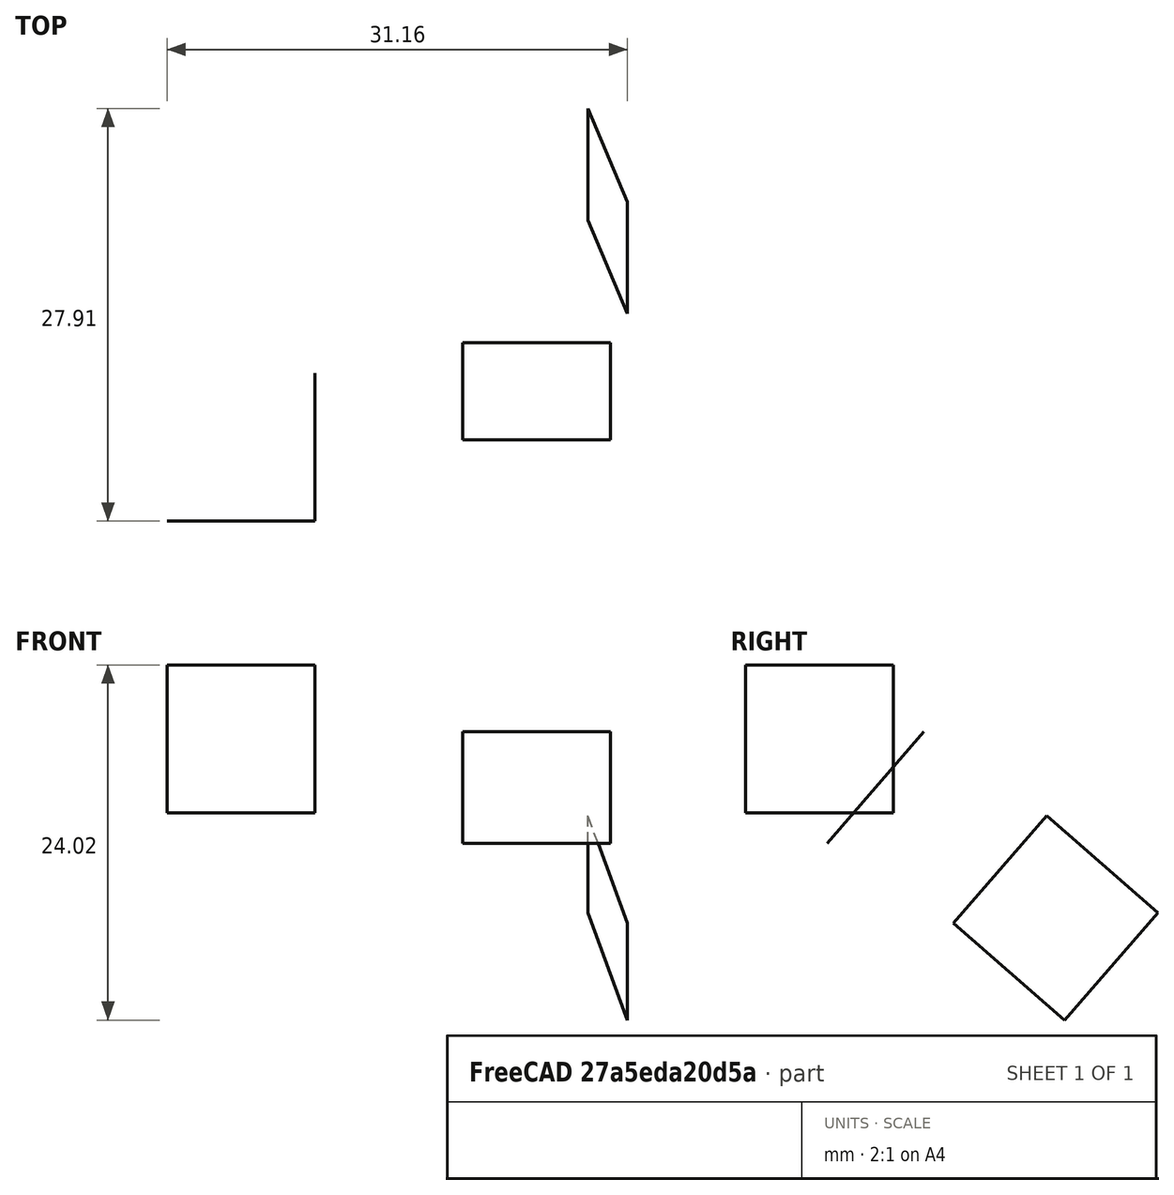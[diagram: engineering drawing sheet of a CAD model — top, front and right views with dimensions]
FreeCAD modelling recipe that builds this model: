
FCSTD DOCUMENT  (FreeCAD 0.19R17089 +1543 (Git))
Label: rt-super-2-c
License: All rights reserved
LicenseURL: http://en.wikipedia.org/wiki/All_rights_reserved
objects: App::FeaturePython×13, Part::FeaturePython×9, App::LinkElement×4, App::Link×1
note: 8 computed .brp shape members not serialized (recipe doc carries the construction recipe); baked Part::Feature solids carry a one-line shape summary decoded from their .brp
EXTERNAL_REF file=rt-super-2-a.FCStd obj=Assembly

FEATURE [App::LinkElement] Link_i0
  LinkedObject = -> <external rt-super-2-a.FCStd>#Assembly
FEATURE [App::LinkElement] Link_i1
  LinkPlacement = pos=(25,4.4e-15,5) rot=(0.672999,0.30683,-0.672999;3.73701rad)
  LinkedObject = -> <external rt-super-2-a.FCStd>#Assembly
  Placement = pos=(25,4.4e-15,5) rot=(0.672999,0.30683,-0.672999;3.73701rad)
FEATURE [App::LinkElement] Link_i2
  LinkPlacement = pos=(20,18.8729,-11.3956) rot=(-0.950073,0.12944,-0.283912;5.38835rad)
  LinkedObject = -> <external rt-super-2-a.FCStd>#Assembly
  Placement = pos=(20,18.8729,-11.3956) rot=(-0.950073,0.12944,-0.283912;5.38835rad)
FEATURE [App::LinkElement] Link_i3
  LinkPlacement = pos=(44.0888,19.4844,-3.06764) rot=(-0.167621,-0.947396,0.272662;1.8739rad)
  LinkedObject = -> <external rt-super-2-a.FCStd>#Assembly
  Placement = pos=(44.0888,19.4844,-3.06764) rot=(-0.167621,-0.947396,0.272662;1.8739rad)
FEATURE [App::Link] Link  label="Super-A"
  ElementCount = 4
  ElementList = -> [Link_i0,Link_i1,Link_i2,Link_i3]
  LinkedObject = -> <external rt-super-2-a.FCStd>#Assembly
FEATURE [Part::FeaturePython] Parts  # WARN: FeaturePython — macro-defined, semantics opaque (R4)
  Group = -> [Link]
  GroupMode = 0
FEATURE [Part::FeaturePython] Assembly  label="Project Assembly Container"  # WARN: FeaturePython — macro-defined, semantics opaque (R4)
  AutoRelax = true
  BuildShape = 0
  Freeze = false
  Group = -> [Constraints,Elements,Parts]
  GroupMode = 1
  SolverType = 1
  Verbose = false
  _SolverType = 1
  _Version = 1
FEATURE [App::FeaturePython] Constraints  # WARN: FeaturePython — macro-defined, semantics opaque (R4)
  Group = -> [Constraint,Constraint001,Constraint002,Constraint003]
  GroupMode = 1
  _Version = 1
FEATURE [App::FeaturePython] Elements  # WARN: FeaturePython — macro-defined, semantics opaque (R4)
  Group = -> [_Element,_Element001,_Element002,_Element003,_Element004,_Element005,_Element006]
  GroupMode = 1
FEATURE [App::FeaturePython] Constraint  label="Locked"  # WARN: FeaturePython — macro-defined, semantics opaque (R4)
  ConstraintType = 0
  Disabled = false
  Group = -> [ElementLink]
  GroupMode = 1
  _ConstraintType = 0
  _Parent = -> Constraints
FEATURE [App::FeaturePython] ElementLink  label="_Element"  # link proxy (typed FeaturePython)
  LinkTransform = true
  LinkedObject = -> _Element
  _Parent = -> Constraint
FEATURE [Part::FeaturePython] _Element  # link proxy (typed FeaturePython)
  Detach = false
  LinkTransform = true
  LinkedObject = -> Link [Link_i0.1.$Public Front.]
  _Parent = -> Elements
FEATURE [App::FeaturePython] Constraint001  label="PlaneCoincident"  # WARN: FeaturePython — macro-defined, semantics opaque (R4)
  Angle = 0
  AnglePitch = 0
  AngleRoll = 0
  Cascade = false
  ConstraintType = 2
  Disabled = false
  Group = -> [ElementLink001,ElementLink002]
  GroupMode = 1
  LockAngle = false
  Multiply = false
  OffsetX = 0
  OffsetY = 0
  _ConstraintType = 35
  _Parent = -> Constraints
FEATURE [App::FeaturePython] ElementLink001  label="_Element001"  # link proxy (typed FeaturePython)
  LinkTransform = true
  LinkedObject = -> _Element001
  _Parent = -> Constraint001
FEATURE [Part::FeaturePython] _Element001  # link proxy (typed FeaturePython)
  Detach = false
  LinkTransform = true
  LinkedObject = -> Link [Link_i0.1.$Public Right.]
  _Parent = -> Elements
FEATURE [App::FeaturePython] ElementLink002  label="_Element002"  # link proxy (typed FeaturePython)
  LinkTransform = true
  LinkedObject = -> _Element002
  _Parent = -> Constraint001
FEATURE [Part::FeaturePython] _Element002  # link proxy (typed FeaturePython)
  Detach = false
  LinkTransform = true
  LinkedObject = -> Link [Link_i1.1.$Cylinder Top.]
  _Parent = -> Elements
FEATURE [App::FeaturePython] Constraint002  label="PlaneCoincident001"  # WARN: FeaturePython — macro-defined, semantics opaque (R4)
  Angle = 0
  AnglePitch = 0
  AngleRoll = 0
  Cascade = false
  ConstraintType = 2
  Disabled = false
  Group = -> [ElementLink003,ElementLink004]
  GroupMode = 1
  LockAngle = false
  Multiply = false
  OffsetX = 0
  OffsetY = 0
  _ConstraintType = 35
  _Parent = -> Constraints
FEATURE [App::FeaturePython] ElementLink003  label="_Element003"  # link proxy (typed FeaturePython)
  LinkTransform = true
  LinkedObject = -> _Element003
  _Parent = -> Constraint002
FEATURE [Part::FeaturePython] _Element003  # link proxy (typed FeaturePython)
  Detach = false
  LinkTransform = true
  LinkedObject = -> Link [Link_i1.1.$Public Right.]
  _Parent = -> Elements
FEATURE [App::FeaturePython] ElementLink004  label="_Element004"  # link proxy (typed FeaturePython)
  LinkTransform = true
  LinkedObject = -> _Element004
  _Parent = -> Constraint002
FEATURE [Part::FeaturePython] _Element004  # link proxy (typed FeaturePython)
  Detach = false
  LinkTransform = true
  LinkedObject = -> Link [Link_i2.1.$Cylinder Top.]
  _Parent = -> Elements
FEATURE [App::FeaturePython] Constraint003  label="PlaneCoincident002"  # WARN: FeaturePython — macro-defined, semantics opaque (R4)
  Angle = 0
  AnglePitch = 0
  AngleRoll = 0
  Cascade = false
  ConstraintType = 2
  Disabled = false
  Group = -> [ElementLink005,ElementLink006]
  GroupMode = 1
  LockAngle = false
  Multiply = false
  OffsetX = 0
  OffsetY = 0
  _ConstraintType = 35
  _Parent = -> Constraints
FEATURE [App::FeaturePython] ElementLink005  label="_Element005"  # link proxy (typed FeaturePython)
  LinkTransform = true
  LinkedObject = -> _Element005
  _Parent = -> Constraint003
FEATURE [Part::FeaturePython] _Element005  # link proxy (typed FeaturePython)
  Detach = false
  LinkTransform = true
  LinkedObject = -> Link [Link_i2.1.$Public Right.]
  _Parent = -> Elements
FEATURE [App::FeaturePython] ElementLink006  label="_Element006"  # link proxy (typed FeaturePython)
  LinkTransform = true
  LinkedObject = -> _Element006
  _Parent = -> Constraint003
FEATURE [Part::FeaturePython] _Element006  # link proxy (typed FeaturePython)
  Detach = false
  LinkTransform = true
  LinkedObject = -> Link [Link_i3.1.$Cylinder Top.]
  _Parent = -> Elements

RESOLVED EXTERNAL PARTS (link-assembly join: the EXTERNAL_REF files above that resolve inside this repo's crawl, each included once):
---- part rt-super-2-a.FCStd = doc fcstd_8dbe8be2ea9f ----
FCSTD DOCUMENT  (FreeCAD 0.19R17089 +1543 (Git))
Label: rt-super-2-a
License: All rights reserved
LicenseURL: http://en.wikipedia.org/wiki/All_rights_reserved
objects: Part::FeaturePython×7, App::FeaturePython×5, Sketcher::SketchObject×2, PartDesign::Pad×2, PartDesign::Body×2
note: 14 computed .brp shape members not serialized (recipe doc carries the construction recipe); baked Part::Feature solids carry a one-line shape summary decoded from their .brp

FEATURE [Sketcher::SketchObject] Sketch
  MapMode = 5
  Support = -> [XY_Plane]
  sketch-geometry (5):
    g0: LineSegment StartX=5 StartY=5 StartZ=0 EndX=-5 EndY=5 EndZ=0
    g1: LineSegment StartX=-5 StartY=5 StartZ=0 EndX=-5 EndY=-5 EndZ=0
    g2: LineSegment StartX=-5 StartY=-5 StartZ=0 EndX=5 EndY=-5 EndZ=0
    g3: LineSegment StartX=5 StartY=-5 StartZ=0 EndX=5 EndY=5 EndZ=0
    g4: Circle [constr] CenterX=0 CenterY=0 CenterZ=0 NormalX=0 NormalY=0 NormalZ=1 AngleXU=0 Radius=7.07107
  constraints (14):
    c: Coincident(g0,g1)
    c: Coincident(g1,g2)
    c: Coincident(g2,g3)
    c: Coincident(g3,g0)
    c: Equal(g0,g1)
    c: Equal(g0,g2)
    c: Equal(g0,g3)
    c: PointOnObject(g0,g4)
    c: PointOnObject(g1,g4)
    c: PointOnObject(g2,g4)
    c: PointOnObject(g3,g4)
    c: Coincident(g4,g-1)
    c: Horizontal(g0)
    c: Distance(g2) = 10
FEATURE [PartDesign::Pad] Pad
  ClaimChildren = false
  Length = 10
  Length2 = 100
  Profile = -> Sketch
  Type = 0
FEATURE [PartDesign::Body] Body  label="Cube 000"
  Group = -> [Sketch,Pad]
  Origin = -> Origin
  Tip = -> Pad
FEATURE [Sketcher::SketchObject] Sketch001
  MapMode = 5
  Support = -> [XY_Plane001]
  sketch-geometry (1):
    g0: Circle CenterX=0 CenterY=0 CenterZ=0 NormalX=0 NormalY=0 NormalZ=1 AngleXU=0 Radius=2.5
  constraints (2):
    c: Coincident(g0,g-1)
    c: Diameter(g0) = 5
FEATURE [PartDesign::Pad] Pad001
  ClaimChildren = false
  Length = 10
  Length2 = 100
  Profile = -> Sketch001
  Type = 0
FEATURE [PartDesign::Body] Body001  label="Cylinder 000"
  Group = -> [Sketch001,Pad001]
  Origin = -> Origin001
  Placement = pos=(0,0,10) rot=(0,0,1;0rad)
  Tip = -> Pad001
FEATURE [Part::FeaturePython] Parts  # WARN: FeaturePython — macro-defined, semantics opaque (R4)
  Group = -> [Body,Body001]
  GroupMode = 0
FEATURE [Part::FeaturePython] Assembly  label="cube-based-000"  # WARN: FeaturePython — macro-defined, semantics opaque (R4)
  AutoRelax = true
  BuildShape = 0
  Freeze = false
  Group = -> [Constraints,Elements,Parts]
  GroupMode = 1
  SolverType = 1
  Verbose = false
  _SolverType = 1
  _Version = 1
FEATURE [App::FeaturePython] Constraints  # WARN: FeaturePython — macro-defined, semantics opaque (R4)
  Group = -> [Constraint]
  GroupMode = 1
  _Version = 1
FEATURE [App::FeaturePython] Elements  # WARN: FeaturePython — macro-defined, semantics opaque (R4)
  Group = -> [Element,Element001,Element002,Element003,Element004]
  GroupMode = 1
FEATURE [Part::FeaturePython] Element  label="Cube Top"  # link proxy (typed FeaturePython)
  Detach = false
  LinkTransform = true
  LinkedObject = -> Body [Pad.Face6]
  _Parent = -> Elements
FEATURE [Part::FeaturePython] Element001  label="Public Right"  # link proxy (typed FeaturePython)
  Detach = false
  LinkTransform = true
  LinkedObject = -> Body [Pad.Face4]
  _Parent = -> Elements
FEATURE [Part::FeaturePython] Element002  label="Public Front"  # link proxy (typed FeaturePython)
  Detach = false
  LinkTransform = true
  LinkedObject = -> Body [Pad.Face3]
  _Parent = -> Elements
FEATURE [Part::FeaturePython] Element003  label="Cylinder Top"  # link proxy (typed FeaturePython)
  Detach = false
  LinkTransform = true
  LinkedObject = -> Body001 [Pad001.Edge3]
  _Parent = -> Elements
FEATURE [Part::FeaturePython] Element004  label="Cylinder Bottom"  # link proxy (typed FeaturePython)
  Detach = false
  LinkTransform = true
  LinkedObject = -> Body001 [Pad001.Edge2]
  _Parent = -> Elements
FEATURE [App::FeaturePython] Constraint  label="PlaneCoincident"  # WARN: FeaturePython — macro-defined, semantics opaque (R4)
  Angle = 0
  AnglePitch = 0
  AngleRoll = 0
  Cascade = false
  ConstraintType = 2
  Disabled = false
  Group = -> [ElementLink,ElementLink001]
  GroupMode = 1
  LockAngle = false
  Multiply = false
  OffsetX = 0
  OffsetY = 0
  _ConstraintType = 35
  _Parent = -> Constraints
FEATURE [App::FeaturePython] ElementLink  label="Cube Top"  # link proxy (typed FeaturePython)
  LinkTransform = true
  LinkedObject = -> Element
  _Parent = -> Constraint
FEATURE [App::FeaturePython] ElementLink001  label="Cylinder Bottom"  # link proxy (typed FeaturePython)
  LinkTransform = true
  LinkedObject = -> Element004
  _Parent = -> Constraint
